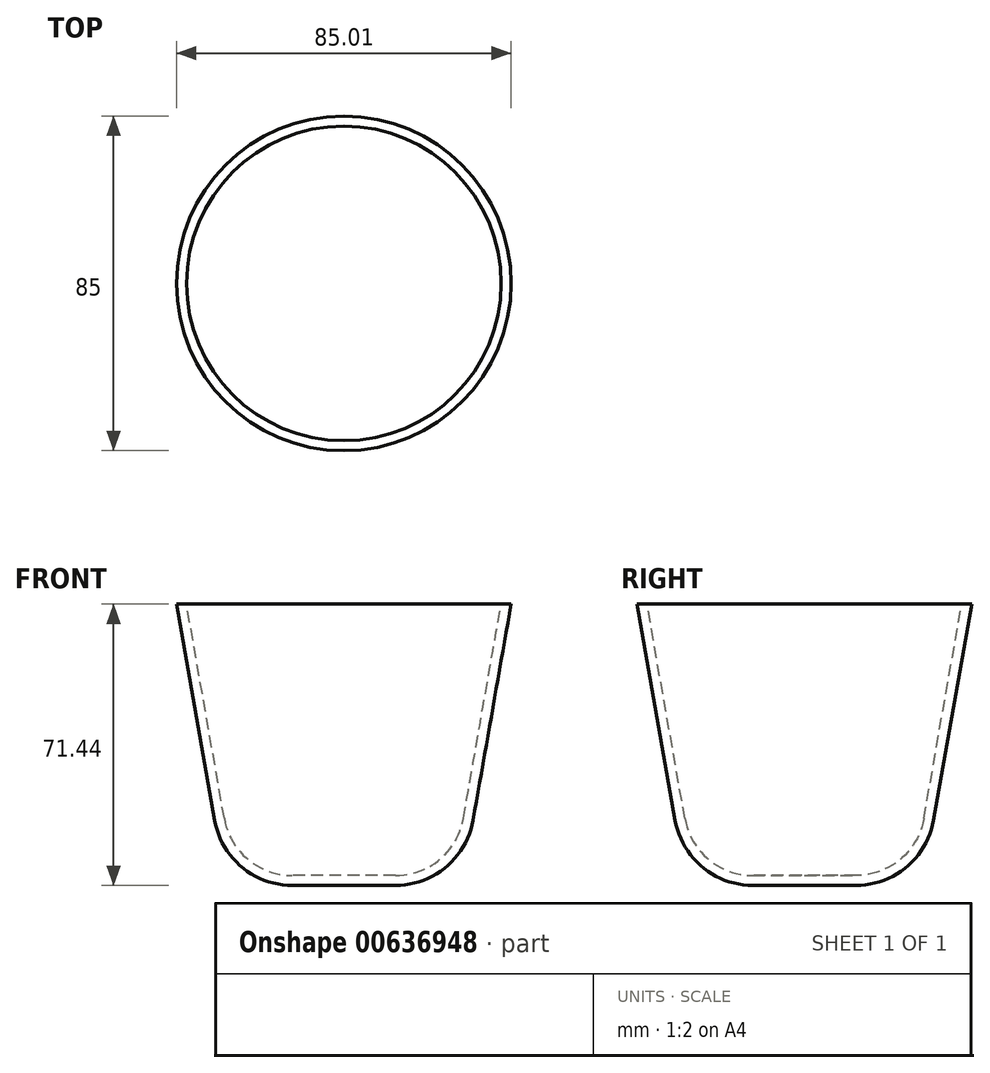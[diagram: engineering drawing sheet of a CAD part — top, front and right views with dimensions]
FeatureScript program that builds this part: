
annotation { "Feature Type Name" : "Feature", "Feature Type Description" : "" }
export const myFeature = defineFeature(function(context is Context, id is Id, definition is map)
    precondition{}
    {
        {
            var Q0;
            Q0=qCreatedBy(makeId("Top.planeOp"),FACE);
            var sketch = newSketch(context, id + "F0", { "sketchPlane" : qUnion([Q0])});
            skCircle(sketch, "E0", {"center": v(40.93, 0) * mm, "radius": 29.9 * mm});
            skSolve(sketch);
        }
        {
            var Q0;
            Q0=makeQuery(id+"F0.imprint","IMPRINT",FACE,{"disambiguationData":[TD([[makeQuery(id+"F0.imprint","IMPRINT",EDGE,{"derivedFrom":sQuery(id+"F0.wireOp",EDGE,"E0")}),1.0]])]});
            extrude(context, id + "F1", {"entities" : qUnion([Q0]), "depth" : 71.44 * mm, "offsetDistance" : 25 * mm, "hasDraft" : true, "draftAngle" : 10 * degree});
        }
        {
            var Q0;
            Q0=makeQuery(id+"F1.opExtrude","CAP_EDGE",EDGE,{"disambiguationData":[OSD([sQuery(id+"F0.wireOp",EDGE,"E0")])],"isStart":true});
            fillet(context, id + "F2", {"entities" : qUnion([Q0]), "radius" : 20 * mm, "tangentPropagation" : true, "allowEdgeOverflow" : false});
        }
        {
            var Q0;
            Q0=makeQuery(id+"F1.opExtrude","CAP_FACE",FACE,{"disambiguationData":[OSD([sQuery(id+"F0.wireOp",EDGE,"E0")])],"isStart":false});
            shell(context, id + "F3", {"entities" : qUnion([Q0]), "thickness" : 2.5 * mm});
        }
    });
